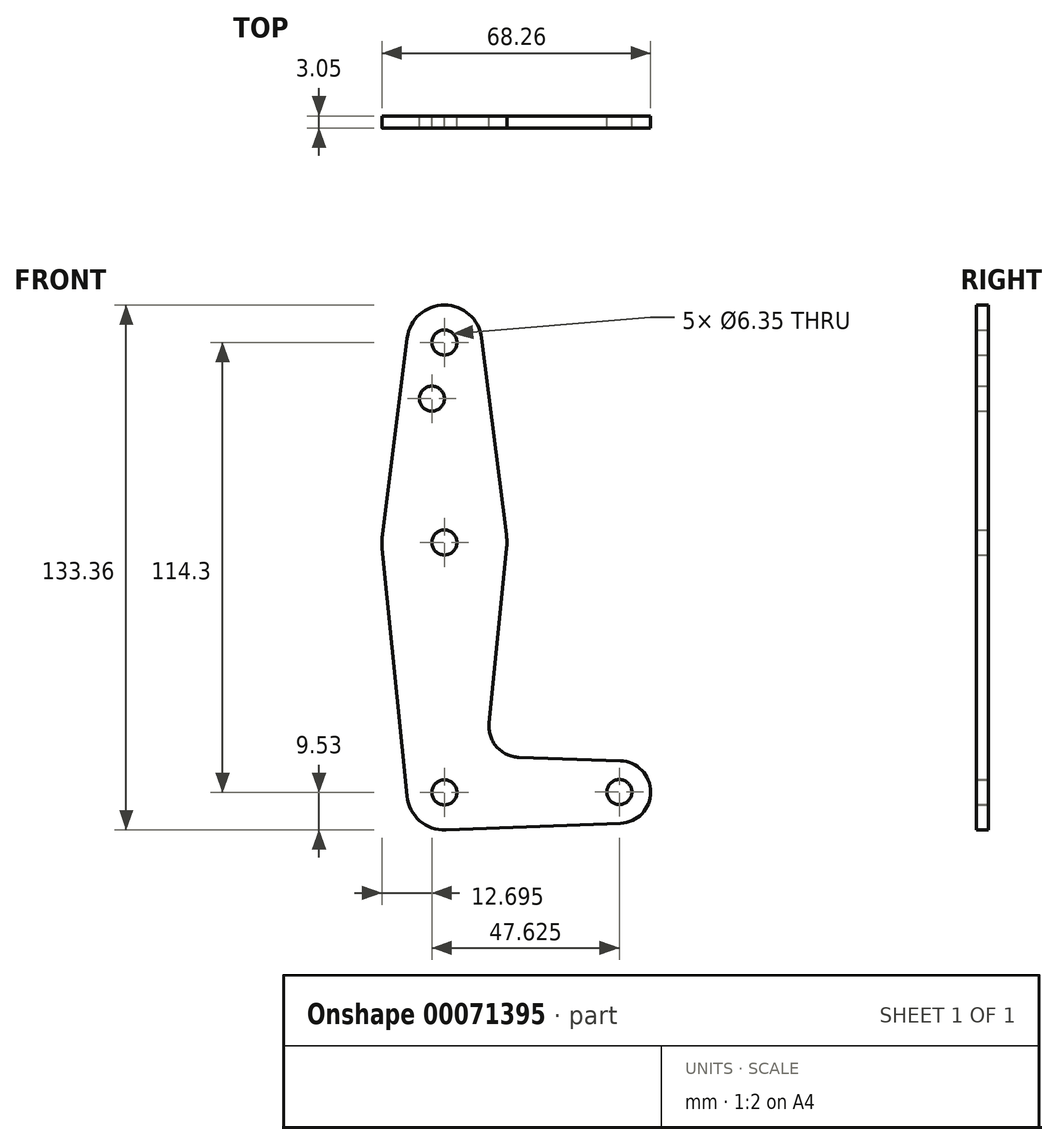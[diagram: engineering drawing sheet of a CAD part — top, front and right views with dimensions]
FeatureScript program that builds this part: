
annotation { "Feature Type Name" : "Feature", "Feature Type Description" : "" }
export const myFeature = defineFeature(function(context is Context, id is Id, definition is map)
    precondition{}
    {
        {
            var Q0;
            Q0=qCreatedBy(makeId("Front.planeOp"),FACE);
            var sketch = newSketch(context, id + "F0", { "sketchPlane" : qUnion([Q0])});
            skCircle(sketch, "E0", {"center": v(0, 114.3) * mm, "radius": 9.53 * mm});
            skCircle(sketch, "E1", {"center": v(0, 63.5) * mm, "radius": 15.88 * mm});
            skLineSegment(sketch, "E2", {"start": v(0, 114.3) * mm, "end": v(0, 0) * mm, "construction": true});
            skLineSegment(sketch, "E3", {"start": v(0, 0) * mm, "end": v(44.45, 0.08) * mm, "construction": true});
            skCircle(sketch, "E4", {"center": v(0, 114.3) * mm, "radius": 3.18 * mm});
            skCircle(sketch, "E5", {"center": v(0, 63.5) * mm, "radius": 3.18 * mm});
            skCircle(sketch, "E6", {"center": v(-3.17, 100.03) * mm, "radius": 3.18 * mm});
            skCircle(sketch, "E7", {"center": v(0, 0) * mm, "radius": 3.18 * mm});
            skCircle(sketch, "E8", {"center": v(44.45, 0.08) * mm, "radius": 3.18 * mm});
            skCircle(sketch, "E9", {"center": v(0, 0) * mm, "radius": 9.53 * mm});
            skCircle(sketch, "E10", {"center": v(44.45, 0.08) * mm, "radius": 7.94 * mm});
            skLineSegment(sketch, "E11", {"start": v(-9.45, 115.5) * mm, "end": v(-15.75, 65.48) * mm});
            skLineSegment(sketch, "E12", {"start": v(9.45, 115.5) * mm, "end": v(15.75, 65.48) * mm});
            skLineSegment(sketch, "E13", {"start": v(15.8, 61.91) * mm, "end": v(11.34, 17.63) * mm});
            skLineSegment(sketch, "E14", {"start": v(-9.48, -0.95) * mm, "end": v(-15.8, 61.91) * mm});
            skLineSegment(sketch, "E15", {"start": v(18.99, 8.89) * mm, "end": v(44.72, 8.01) * mm});
            skLineSegment(sketch, "E16", {"start": v(44.75, -7.85) * mm, "end": v(0.36, -9.52) * mm});
            skPoint(sketch, "E17.newPointA", {"position": v(9.48, -0.95) * mm});
            skArc(sketch, "E17.filletArc", {"start": v(11.34, 17.63) * mm, "mid": v(13.27, 11.6) * mm, "end": v(18.99, 8.89) * mm});
            skSolve(sketch);
        }
        {
            var Q0;
            Q0 = qSketchRegion(id + "F0", true);
            extrude(context, id + "F1", {"entities" : qUnion([Q0]), "depth" : 3.05 * mm});
        }
    });
